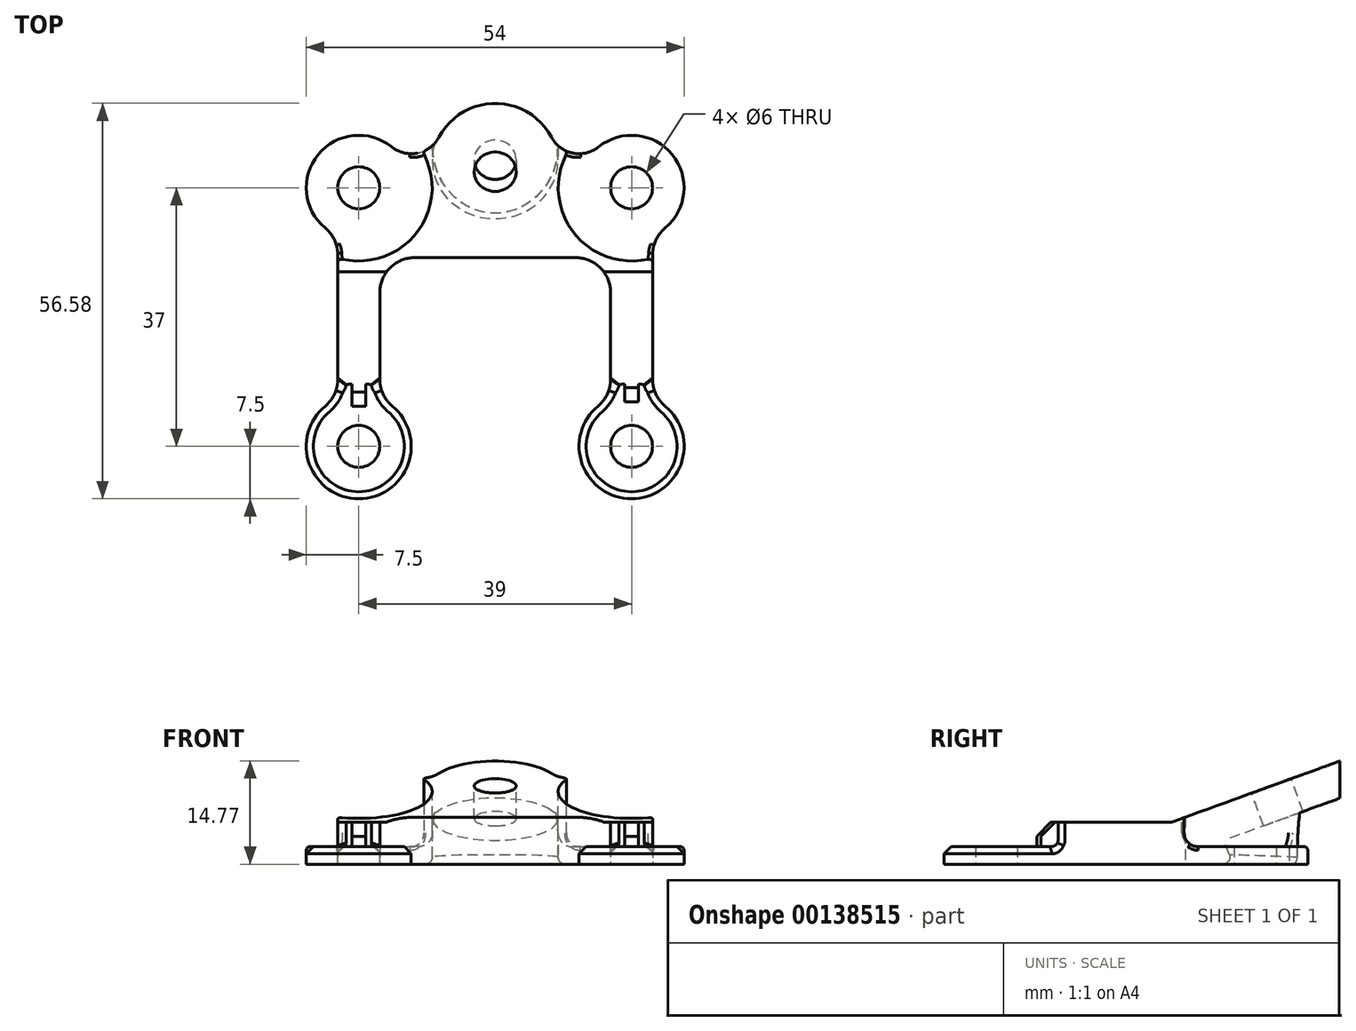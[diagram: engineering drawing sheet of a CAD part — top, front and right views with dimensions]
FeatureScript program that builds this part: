
annotation { "Feature Type Name" : "Feature", "Feature Type Description" : "" }
export const myFeature = defineFeature(function(context is Context, id is Id, definition is map)
    precondition{}
    {
        {
            var Q0;
            Q0=qCreatedBy(makeId("Top.planeOp"),FACE);
            var sketch = newSketch(context, id + "F0", { "sketchPlane" : qUnion([Q0])});
            skCircle(sketch, "E0", {"center": v(0, 0) * mm, "radius": 3 * mm});
            skCircle(sketch, "E1", {"center": v(39, 0) * mm, "radius": 3 * mm});
            skCircle(sketch, "E2", {"center": v(39, 37) * mm, "radius": 3 * mm});
            skCircle(sketch, "E3", {"center": v(0, 37) * mm, "radius": 3 * mm});
            skArc(sketch, "E4", {"start": v(4.69, 42.85) * mm, "mid": v(-6.42, 40.88) * mm, "end": v(-3, 30.13) * mm});
            skArc(sketch, "E5", {"start": v(42, 30.13) * mm, "mid": v(45.42, 40.88) * mm, "end": v(34.31, 42.85) * mm});
            skArc(sketch, "E6", {"start": v(36, 6.87) * mm, "mid": v(39, -7.5) * mm, "end": v(42, 6.87) * mm});
            skArc(sketch, "E7", {"start": v(-3, 6.87) * mm, "mid": v(0, -7.5) * mm, "end": v(3, 6.87) * mm});
            skArc(sketch, "E8", {"start": v(27.52, 44.26) * mm, "mid": v(19.5, 49.08) * mm, "end": v(11.48, 44.26) * mm});
            skArc(sketch, "E9", {"start": v(4.69, 42.85) * mm, "mid": v(8.41, 41.96) * mm, "end": v(11.48, 44.26) * mm});
            skLineSegment(sketch, "E10.top", {"start": v(3, 27) * mm, "end": v(36, 27) * mm});
            skLineSegment(sketch, "E10.left", {"start": v(3, 6.87) * mm, "end": v(3, 27) * mm});
            skLineSegment(sketch, "E10.right", {"start": v(36, 6.87) * mm, "end": v(36, 27) * mm});
            skLineSegment(sketch, "E11", {"start": v(19.5, 40) * mm, "end": v(19.5, -9.5) * mm, "construction": true});
            skArc(sketch, "E12.MirrorC", {"start": v(34.31, 42.85) * mm, "mid": v(30.59, 41.96) * mm, "end": v(27.52, 44.26) * mm});
            skLineSegment(sketch, "E13.trimOffspring", {"start": v(-3, 30.13) * mm, "end": v(-3, 6.87) * mm});
            skPoint(sketch, "E14.orphan", {"position": v(-3, 40) * mm});
            skLineSegment(sketch, "E15.trimOffspring", {"start": v(42, 30.13) * mm, "end": v(42, 6.87) * mm});
            skPoint(sketch, "E16.right.start.orphan", {"position": v(42, 40) * mm});
            skPoint(sketch, "E17.orphan", {"position": v(3, 0) * mm});
            skSolve(sketch);
        }
        {
            var Q0;
            Q0=makeQuery(id+"F0.imprint","IMPRINT",FACE,{"disambiguationData":[TD([[makeQuery(id+"F0.imprint","IMPRINT",EDGE,{"derivedFrom":sQuery(id+"F0.wireOp",EDGE,"E0")}),-1.0]])]});
            extrude(context, id + "F1", {"entities" : qUnion([Q0]), "depth" : 25 * mm});
        }
        {
            var Q0;
            Q0=makeQuery(id+"F1.opExtrude","SWEPT_EDGE",EDGE,{"disambiguationData":[OSD([sQuery(id+"F0.wireOp",EDGE,"E10.top"),sQuery(id+"F0.wireOp",EDGE,"E10.left")])]});
            var Q1;
            Q1=makeQuery(id+"F1.opExtrude","SWEPT_EDGE",EDGE,{"disambiguationData":[OSD([sQuery(id+"F0.wireOp",EDGE,"E10.top"),sQuery(id+"F0.wireOp",EDGE,"E10.right")])]});
            var Q2;
            Q2=makeQuery(id+"F1.opExtrude","SWEPT_EDGE",EDGE,{"disambiguationData":[OSD([sQuery(id+"F0.wireOp",EDGE,"E5"),sQuery(id+"F0.wireOp",EDGE,"E15.trimOffspring")])]});
            var Q3;
            Q3=makeQuery(id+"F1.opExtrude","SWEPT_EDGE",EDGE,{"disambiguationData":[OSD([sQuery(id+"F0.wireOp",EDGE,"E6"),sQuery(id+"F0.wireOp",EDGE,"E15.trimOffspring")])]});
            var Q4;
            Q4=makeQuery(id+"F1.opExtrude","SWEPT_EDGE",EDGE,{"disambiguationData":[OSD([sQuery(id+"F0.wireOp",EDGE,"E6"),sQuery(id+"F0.wireOp",EDGE,"E10.right")])]});
            var Q5;
            Q5=makeQuery(id+"F1.opExtrude","SWEPT_EDGE",EDGE,{"disambiguationData":[OSD([sQuery(id+"F0.wireOp",EDGE,"E7"),sQuery(id+"F0.wireOp",EDGE,"E10.left")])]});
            var Q6;
            Q6=makeQuery(id+"F1.opExtrude","SWEPT_EDGE",EDGE,{"disambiguationData":[OSD([sQuery(id+"F0.wireOp",EDGE,"E4"),sQuery(id+"F0.wireOp",EDGE,"E13.trimOffspring")])]});
            var Q7;
            Q7=makeQuery(id+"F1.opExtrude","SWEPT_EDGE",EDGE,{"disambiguationData":[OSD([sQuery(id+"F0.wireOp",EDGE,"E7"),sQuery(id+"F0.wireOp",EDGE,"E13.trimOffspring")])]});
            fillet(context, id + "F2", {"entities" : qUnion([Q0, Q1, Q2, Q3, Q4, Q5, Q6, Q7]), "radius" : 5 * mm, "tangentPropagation" : true, "allowEdgeOverflow" : false});
        }
        {
            var Q0;
            Q0=qCreatedBy(makeId("Right.planeOp"),FACE);
            var sketch = newSketch(context, id + "F3", { "sketchPlane" : qUnion([Q0])});
            skLineSegment(sketch, "E18", {"start": v(51, 15.46) * mm, "end": v(25, 6) * mm});
            skLineSegment(sketch, "E19", {"start": v(25, 6) * mm, "end": v(-9, 6) * mm});
            skLineSegment(sketch, "E20", {"start": v(-9, 6) * mm, "end": v(-9, 30) * mm});
            skLineSegment(sketch, "E21", {"start": v(-9, 30) * mm, "end": v(51, 30) * mm});
            skLineSegment(sketch, "E22", {"start": v(51, 15.46) * mm, "end": v(51, 30) * mm});
            skSolve(sketch);
        }
        {
            var Q0;
            Q0=makeQuery(id+"F3.imprint","IMPRINT",FACE,{"disambiguationData":[TD([[makeQuery(id+"F3.imprint","IMPRINT",EDGE,{"derivedFrom":sQuery(id+"F3.wireOp",EDGE,"E18")}),-1.0]])]});
            extrude(context, id + "F4", {"entities" : qUnion([Q0]), "operationType" : NewBodyOperationType.REMOVE, "oppositeDirection" : true, "depth" : 25 * mm, "hasSecondDirection" : true, "secondDirectionOppositeDirection" : false, "secondDirectionDepth" : 63.98 * mm});
        }
        {
            var Q0;
            Q0=makeQuery(id+"F4.boolean.opBoolean","COPY",FACE,{"derivedFrom":makeQuery(id+"F4.opExtrude","SWEPT_FACE",FACE,{"disambiguationData":[OSD([sQuery(id+"F3.wireOp",EDGE,"E18")])]})});
            var sketch = newSketch(context, id + "F5", { "sketchPlane" : qUnion([Q0])});
            skCircle(sketch, "E23", {"center": v(19.5, 40.76) * mm, "radius": 3 * mm});
            skPoint(sketch, "E23.centerSnap0", {"position": v(19.5, 51.17) * mm});
            skSolve(sketch);
        }
        {
            var Q0;
            Q0 = qSketchRegion(id + "F5", true);
            extrude(context, id + "F6", {"entities" : qUnion([Q0]), "operationType" : NewBodyOperationType.REMOVE, "oppositeDirection" : true, "depth" : 25 * mm});
        }
        {
            var Q0;
            Q0=makeQuery(id+"F4.boolean.opBoolean","COPY",FACE,{"derivedFrom":makeQuery(id+"F4.opExtrude","SWEPT_FACE",FACE,{"disambiguationData":[OSD([sQuery(id+"F3.wireOp",EDGE,"E18")])]})});
            cPlane(context, id + "F7", {"entities" : qUnion([Q0]), "cplaneType" : CPlaneType.OFFSET, "offset" : 5 * mm, "oppositeDirection" : true, "width" : 150 * mm, "height" : 150 * mm});
        }
        {
            var Q0;
            Q0=qCreatedBy(id+"F7.planeOp",FACE);
            var sketch = newSketch(context, id + "F8", { "sketchPlane" : qUnion([Q0])});
            skCircle(sketch, "E24", {"center": v(19.5, 40.76) * mm, "radius": 9 * mm});
            skSolve(sketch);
        }
        {
            var Q0;
            Q0=makeQuery(id+"F8.imprint","IMPRINT",FACE,{"disambiguationData":[TD([[makeQuery(id+"F8.imprint","IMPRINT",EDGE,{"derivedFrom":sQuery(id+"F8.wireOp",EDGE,"E24")}),1.0]])]});
            extrude(context, id + "F9", {"entities" : qUnion([Q0]), "operationType" : NewBodyOperationType.REMOVE, "oppositeDirection" : true, "depth" : 25 * mm});
        }
        {
            var Q0;
            Q0=makeQuery(id+"F4.boolean.opBoolean","COPY",FACE,{"disambiguationData":[TD([makeQuery(id+"F1.opExtrude","SWEPT_FACE",FACE,{"disambiguationData":[OSD([sQuery(id+"F0.wireOp",EDGE,"E0")])]})])],"derivedFrom":makeQuery(id+"F4.opExtrude","SWEPT_FACE",FACE,{"disambiguationData":[OSD([sQuery(id+"F3.wireOp",EDGE,"E19")])]})});
            var sketch = newSketch(context, id + "F10", { "sketchPlane" : qUnion([Q0])});
            skCircle(sketch, "E25", {"center": v(0, 0) * mm, "radius": 9 * mm});
            skCircle(sketch, "E26", {"center": v(39, 0) * mm, "radius": 9 * mm});
            skCircle(sketch, "E27", {"center": v(0, 37) * mm, "radius": 10.5 * mm});
            skCircle(sketch, "E28", {"center": v(39, 37) * mm, "radius": 10.5 * mm});
            skSolve(sketch);
        }
        {
            var Q0;
            Q0 = qSketchRegion(id + "F10", true);
            extrude(context, id + "F11", {"entities" : qUnion([Q0]), "operationType" : NewBodyOperationType.REMOVE, "oppositeDirection" : true, "depth" : 3.5 * mm, "hasSecondDirection" : true, "secondDirectionOppositeDirection" : false, "secondDirectionDepth" : 25 * mm});
        }
        {
            var Q0;
            Q0=makeQuery(id+"F11.boolean.opBoolean","COPY",EDGE,{"derivedFrom":makeQuery(id+"F11.opExtrude","CAP_EDGE",EDGE,{"disambiguationData":[OSD([sQuery(id+"F10.wireOp",EDGE,"E27")])],"isStart":false})});
            var Q1;
            Q1=makeQuery(id+"F11.boolean.opBoolean","COPY",EDGE,{"derivedFrom":makeQuery(id+"F11.opExtrude","CAP_EDGE",EDGE,{"disambiguationData":[OSD([sQuery(id+"F10.wireOp",EDGE,"E28")])],"isStart":false})});
            fillet(context, id + "F12", {"entities" : qUnion([Q0, Q1]), "radius" : 2 * mm, "tangentPropagation" : true, "allowEdgeOverflow" : false});
        }
        {
            var Q0;
            Q0=makeQuery(id+"F11.boolean.opBoolean","COPY",EDGE,{"derivedFrom":makeQuery(id+"F11.opExtrude","CAP_EDGE",EDGE,{"disambiguationData":[OSD([sQuery(id+"F10.wireOp",EDGE,"E26")])],"isStart":false})});
            var Q1;
            Q1=makeQuery(id+"F11.boolean.opBoolean","COPY",EDGE,{"derivedFrom":makeQuery(id+"F11.opExtrude","CAP_EDGE",EDGE,{"disambiguationData":[OSD([sQuery(id+"F10.wireOp",EDGE,"E25")])],"isStart":false})});
            fillet(context, id + "F13", {"entities" : qUnion([Q0, Q1]), "radius" : 1 * mm, "tangentPropagation" : true, "allowEdgeOverflow" : false});
        }
        {
            var Q0;
            Q0=makeQuery(id+"F11.boolean.opBoolean","INTERSECT",EDGE,{"derivedFrom":[makeQuery(id+"F1.opExtrude","SWEPT_FACE",FACE,{"disambiguationData":[OSD([sQuery(id+"F0.wireOp",EDGE,"E12.MirrorC")])]}),makeQuery(id+"F11.opExtrude","SWEPT_FACE",FACE,{"disambiguationData":[OSD([sQuery(id+"F10.wireOp",EDGE,"E28")])]})]});
            var Q1;
            Q1=makeQuery(id+"F11.boolean.opBoolean","INTERSECT",EDGE,{"derivedFrom":[makeQuery(id+"F1.opExtrude","SWEPT_FACE",FACE,{"disambiguationData":[OSD([sQuery(id+"F0.wireOp",EDGE,"E9")])]}),makeQuery(id+"F11.opExtrude","SWEPT_FACE",FACE,{"disambiguationData":[OSD([sQuery(id+"F10.wireOp",EDGE,"E27")])]})]});
            fillet(context, id + "F14", {"entities" : qUnion([Q0, Q1]), "radius" : .5 * mm, "tangentPropagation" : true, "allowEdgeOverflow" : false});
        }
        {
            var Q0;
            Q0=makeQuery(id+"F9.boolean.opBoolean","INTERSECT",EDGE,{"derivedFrom":[makeQuery(id+"F1.opExtrude","CAP_FACE",FACE,{"disambiguationData":[OSD([sQuery(id+"F0.wireOp",EDGE,"E0"),sQuery(id+"F0.wireOp",EDGE,"E1"),sQuery(id+"F0.wireOp",EDGE,"E2"),sQuery(id+"F0.wireOp",EDGE,"E3"),sQuery(id+"F0.wireOp",EDGE,"E4"),sQuery(id+"F0.wireOp",EDGE,"E5"),sQuery(id+"F0.wireOp",EDGE,"E6"),sQuery(id+"F0.wireOp",EDGE,"E7"),sQuery(id+"F0.wireOp",EDGE,"E8"),sQuery(id+"F0.wireOp",EDGE,"E9"),sQuery(id+"F0.wireOp",EDGE,"E10.top"),sQuery(id+"F0.wireOp",EDGE,"E10.left"),sQuery(id+"F0.wireOp",EDGE,"E10.right"),sQuery(id+"F0.wireOp",EDGE,"E12.MirrorC"),sQuery(id+"F0.wireOp",EDGE,"E13.trimOffspring"),sQuery(id+"F0.wireOp",EDGE,"E15.trimOffspring")])],"isStart":true}),makeQuery(id+"F9.opExtrude","SWEPT_FACE",FACE,{"disambiguationData":[OSD([sQuery(id+"F8.wireOp",EDGE,"E24")])]})]});
            fillet(context, id + "F15", {"entities" : qUnion([Q0]), "radius" : 1 * mm, "tangentPropagation" : true, "allowEdgeOverflow" : false});
        }
        {
            var Q0;
            Q0=makeQuery(id+"F11.boolean.opBoolean","COPY",FACE,{"derivedFrom":makeQuery(id+"F11.opExtrude","CAP_FACE",FACE,{"disambiguationData":[OSD([sQuery(id+"F10.wireOp",EDGE,"E25")])],"isStart":false})});
            var sketch = newSketch(context, id + "F16", { "sketchPlane" : qUnion([Q0])});
            skLineSegment(sketch, "E29.bottom", {"start": v(-1, 5.76) * mm, "end": v(1, 5.76) * mm});
            skLineSegment(sketch, "E29.top", {"start": v(-1, 10.27) * mm, "end": v(1, 10.27) * mm});
            skLineSegment(sketch, "E29.left", {"start": v(-1, 5.76) * mm, "end": v(-1, 10.27) * mm});
            skLineSegment(sketch, "E29.right", {"start": v(1, 5.76) * mm, "end": v(1, 10.27) * mm});
            skPoint(sketch, "E30.firstSnap0", {"position": v(4.17, 6.39) * mm});
            skLineSegment(sketch, "E30.bottom", {"start": v(38, 6.39) * mm, "end": v(40, 6.39) * mm});
            skLineSegment(sketch, "E30.top", {"start": v(38, 11.67) * mm, "end": v(40, 11.67) * mm});
            skLineSegment(sketch, "E30.left", {"start": v(38, 6.39) * mm, "end": v(38, 11.67) * mm});
            skLineSegment(sketch, "E30.right", {"start": v(40, 6.39) * mm, "end": v(40, 11.67) * mm});
            skSolve(sketch);
        }
        {
            var Q0;
            Q0 = qSketchRegion(id + "F16", true);
            extrude(context, id + "F17", {"entities" : qUnion([Q0]), "operationType" : NewBodyOperationType.ADD, "depth" : 3.5 * mm});
        }
        {
            var Q0;
            Q0=makeQuery(id+"F17.opExtrude","CAP_EDGE",EDGE,{"disambiguationData":[OSD([sQuery(id+"F16.wireOp",EDGE,"E29.bottom")])],"isStart":false});
            var Q1;
            Q1=makeQuery(id+"F17.opExtrude","CAP_EDGE",EDGE,{"disambiguationData":[OSD([sQuery(id+"F16.wireOp",EDGE,"E30.bottom")])],"isStart":false});
            chamfer(context, id + "F18", {"entities" : qUnion([Q0, Q1]), "width" : 2 * mm, "tangentPropagation" : true});
        }
        {
            var Q0;
            Q0=makeQuery(id+"F11.boolean.opBoolean","INTERSECT",EDGE,{"derivedFrom":[makeQuery(id+"F1.opExtrude","SWEPT_FACE",FACE,{"disambiguationData":[OSD([sQuery(id+"F0.wireOp",EDGE,"E7")])]}),makeQuery(id+"F11.opExtrude","CAP_FACE",FACE,{"disambiguationData":[OSD([sQuery(id+"F10.wireOp",EDGE,"E25")])],"isStart":false})]});
            var Q1;
            Q1=makeQuery(id+"F11.boolean.opBoolean","INTERSECT",EDGE,{"derivedFrom":[makeQuery(id+"F1.opExtrude","SWEPT_FACE",FACE,{"disambiguationData":[OSD([sQuery(id+"F0.wireOp",EDGE,"E6")])]}),makeQuery(id+"F11.opExtrude","CAP_FACE",FACE,{"disambiguationData":[OSD([sQuery(id+"F10.wireOp",EDGE,"E26")])],"isStart":false})]});
            chamfer(context, id + "F19", {"entities" : qUnion([Q0, Q1]), "width" : 1 * mm, "tangentPropagation" : true});
        }
    });
